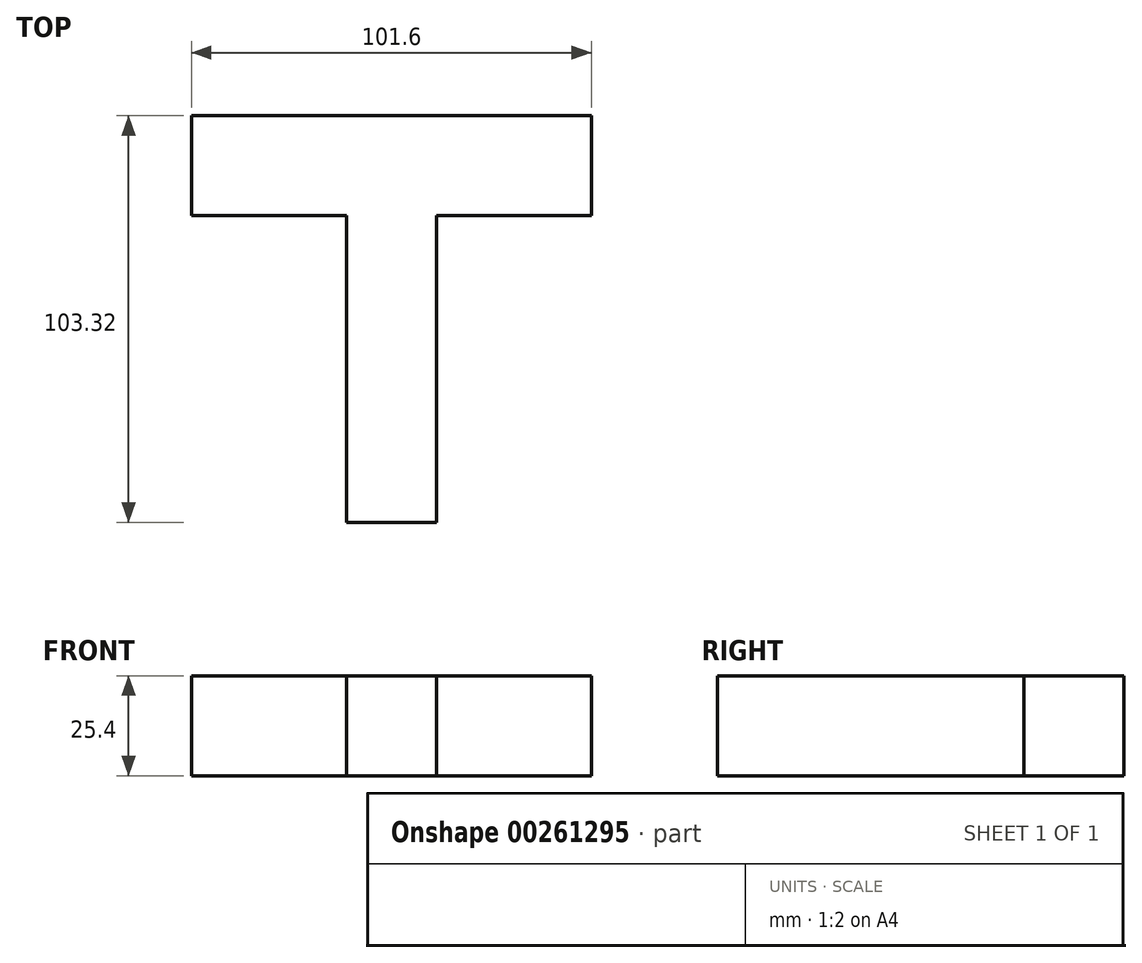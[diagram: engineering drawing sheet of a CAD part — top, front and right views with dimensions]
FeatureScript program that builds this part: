
annotation { "Feature Type Name" : "Feature", "Feature Type Description" : "" }
export const myFeature = defineFeature(function(context is Context, id is Id, definition is map)
    precondition{}
    {
        {
            var Q0;
            Q0=qCreatedBy(makeId("Top.planeOp"),FACE);
            var sketch = newSketch(context, id + "F0", { "sketchPlane" : qUnion([Q0])});
            skLineSegment(sketch, "E0.bottom", {"start": v(11.43, -51.66) * mm, "end": v(-11.43, -51.66) * mm});
            skLineSegment(sketch, "E0.top", {"start": v(11.43, 51.66) * mm, "end": v(-11.43, 51.66) * mm});
            skLineSegment(sketch, "E0.left", {"start": v(11.43, -51.66) * mm, "end": v(11.43, 51.66) * mm});
            skLineSegment(sketch, "E0.right", {"start": v(-11.43, -51.66) * mm, "end": v(-11.43, 51.66) * mm});
            skPoint(sketch, "E0.middle", {"position": v(0, 0) * mm});
            skLineSegment(sketch, "E1.bottom", {"start": v(-50.8, 51.66) * mm, "end": v(50.8, 51.66) * mm});
            skLineSegment(sketch, "E1.top", {"start": v(-50.8, 26.26) * mm, "end": v(50.8, 26.26) * mm});
            skLineSegment(sketch, "E1.left", {"start": v(-50.8, 51.66) * mm, "end": v(-50.8, 26.26) * mm});
            skLineSegment(sketch, "E1.right", {"start": v(50.8, 51.66) * mm, "end": v(50.8, 26.26) * mm});
            skSolve(sketch);
        }
        {
            var Q0;
            Q0 = qSketchRegion(id + "F0", true);
            extrude(context, id + "F1", {"entities" : qUnion([Q0]), "depth" : 25.4 * mm});
        }
    });
